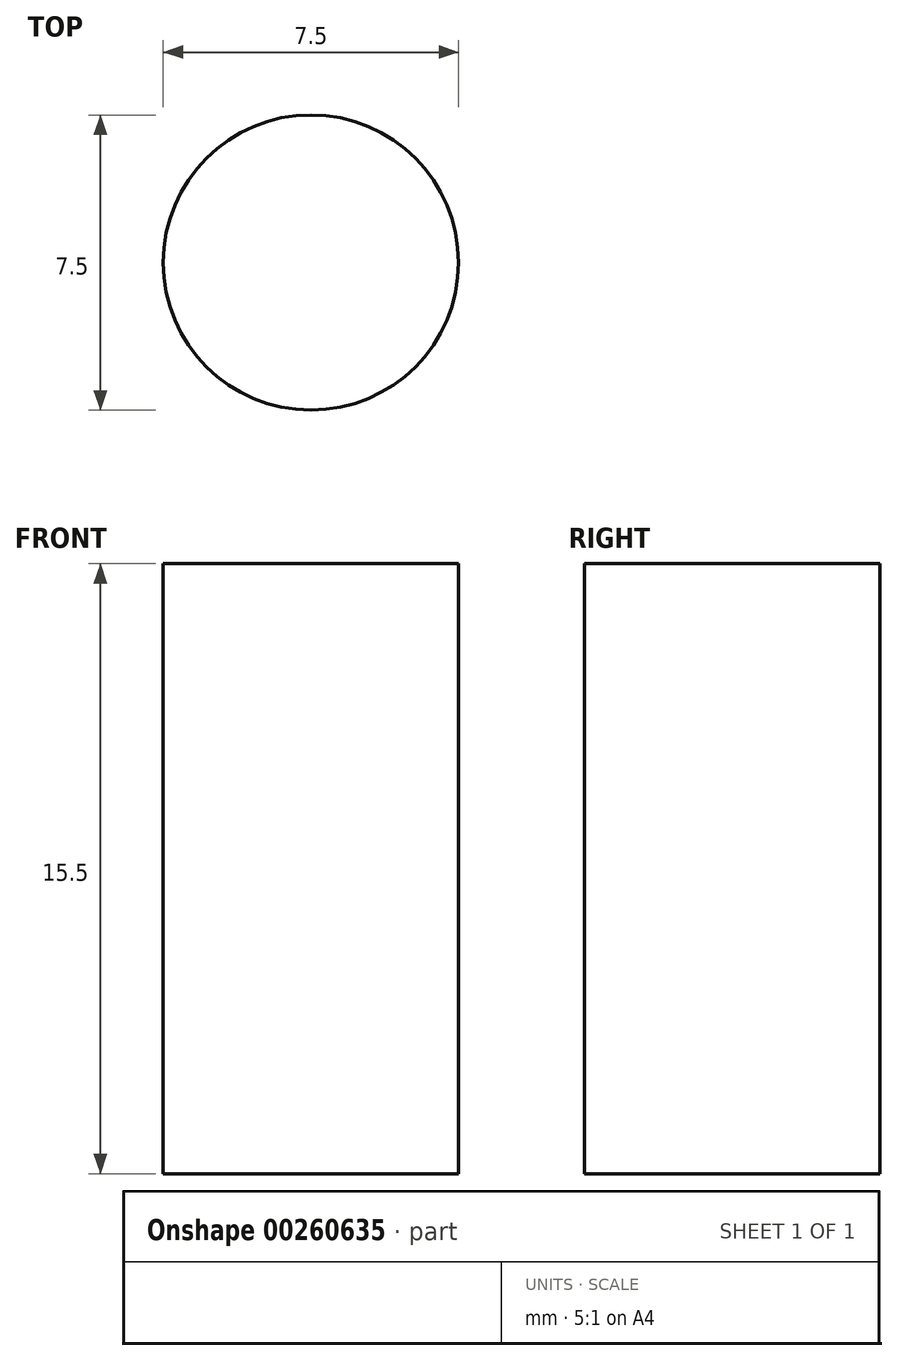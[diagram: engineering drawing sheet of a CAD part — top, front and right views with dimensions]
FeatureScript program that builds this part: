
annotation { "Feature Type Name" : "Feature", "Feature Type Description" : "" }
export const myFeature = defineFeature(function(context is Context, id is Id, definition is map)
    precondition{}
    {
        {
            var Q0;
            Q0=qCreatedBy(makeId("Top.planeOp"),FACE);
            var sketch = newSketch(context, id + "F0", { "sketchPlane" : qUnion([Q0])});
            skCircle(sketch, "E0", {"center": v(0, 0) * mm, "radius": 3.75 * mm});
            skSolve(sketch);
        }
        {
            var Q0;
            Q0 = qSketchRegion(id + "F0", true);
            extrude(context, id + "F1", {"entities" : qUnion([Q0]), "depth" : 15.5 * mm});
        }
    });
